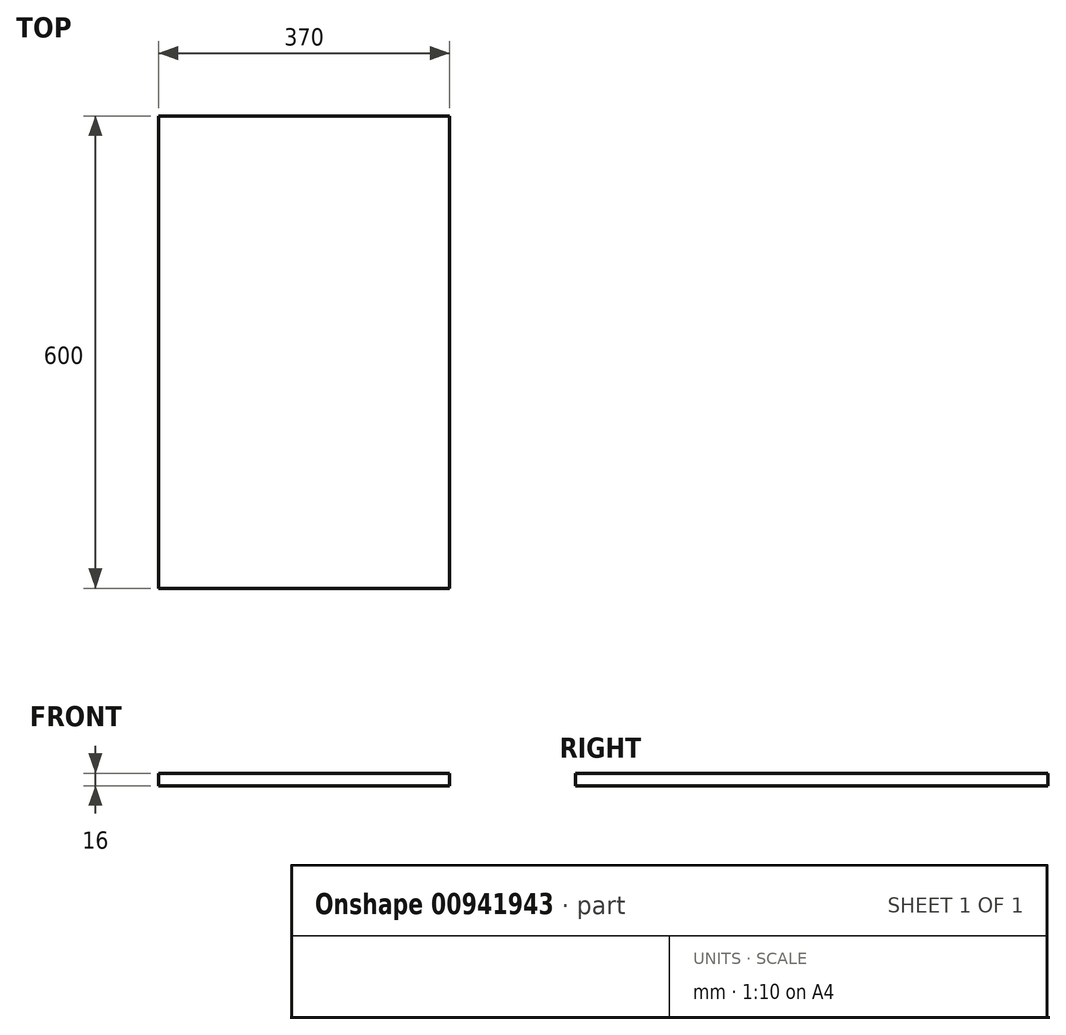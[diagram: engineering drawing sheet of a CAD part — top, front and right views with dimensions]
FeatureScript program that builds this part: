
annotation { "Feature Type Name" : "Feature", "Feature Type Description" : "" }
export const myFeature = defineFeature(function(context is Context, id is Id, definition is map)
    precondition{}
    {
        {
            var Q0;
            Q0=qCreatedBy(makeId("Top.planeOp"),FACE);
            var sketch = newSketch(context, id + "F0", { "sketchPlane" : qUnion([Q0])});
            skLineSegment(sketch, "E0.bottom", {"start": v(0, 0) * mm, "end": v(370, 0) * mm});
            skLineSegment(sketch, "E0.top", {"start": v(0, -600) * mm, "end": v(370, -600) * mm});
            skLineSegment(sketch, "E0.left", {"start": v(0, 0) * mm, "end": v(0, -600) * mm});
            skLineSegment(sketch, "E0.right", {"start": v(370, 0) * mm, "end": v(370, -600) * mm});
            skSolve(sketch);
        }
        {
            var Q0;
            Q0 = qSketchRegion(id + "F0", true);
            extrude(context, id + "F1", {"entities" : qUnion([Q0]), "depth" : 16 * mm, "offsetDistance" : 25 * mm});
        }
    });
